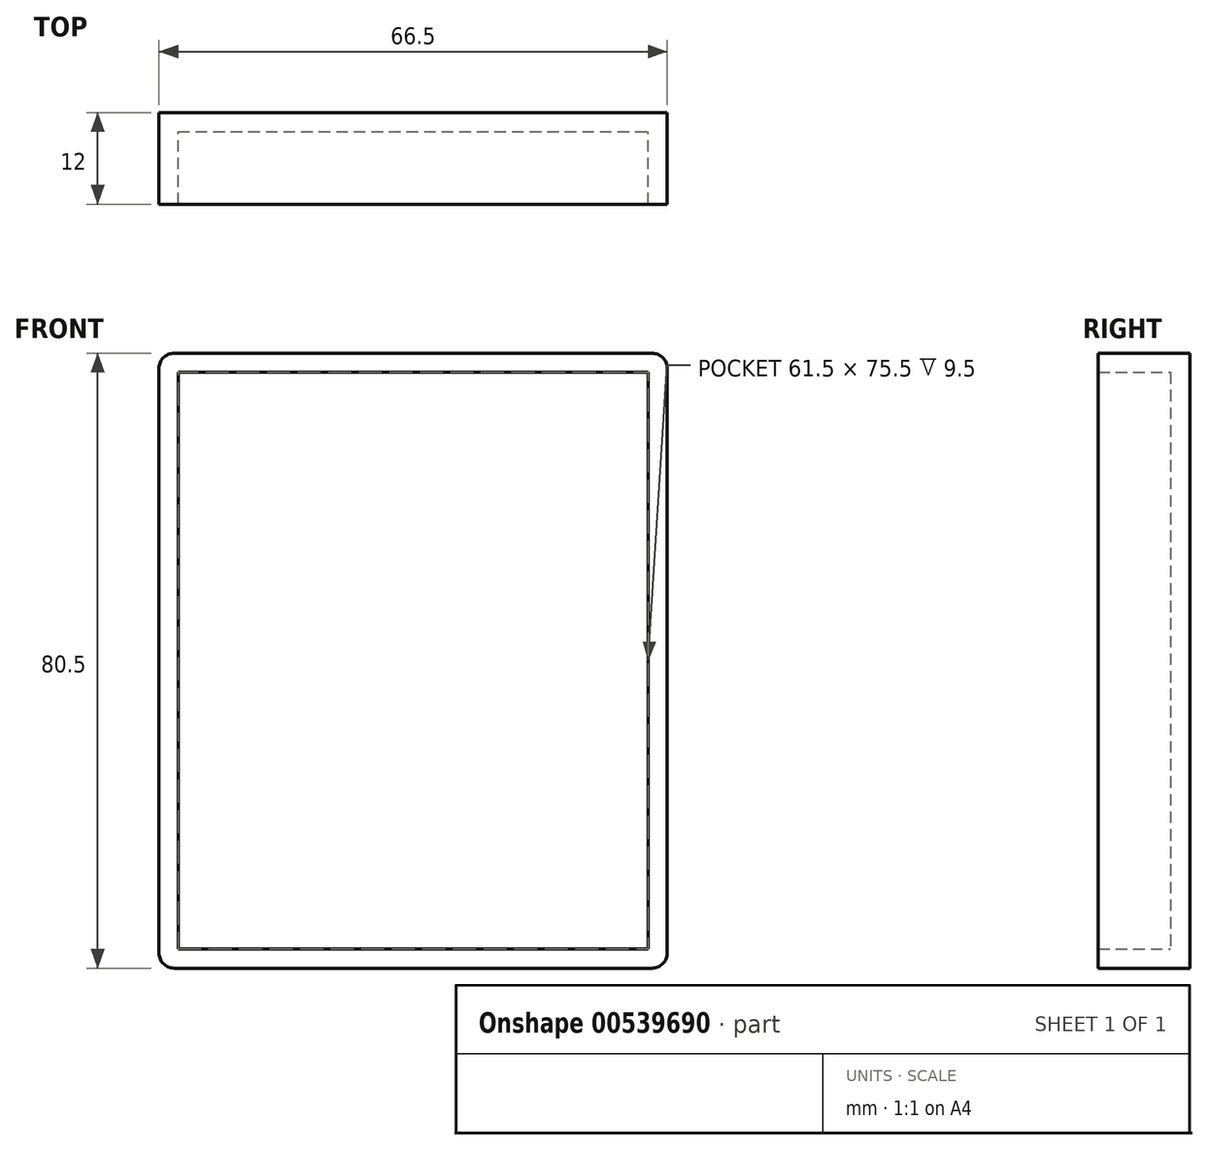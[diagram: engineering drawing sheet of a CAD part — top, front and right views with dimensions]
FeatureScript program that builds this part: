
annotation { "Feature Type Name" : "Feature", "Feature Type Description" : "" }
export const myFeature = defineFeature(function(context is Context, id is Id, definition is map)
    precondition{}
    {
        {
            var Q0;
            Q0=qCreatedBy(makeId("Front.planeOp"),FACE);
            var sketch = newSketch(context, id + "F0", { "sketchPlane" : qUnion([Q0])});
            skLineSegment(sketch, "E0.bottom", {"start": v(-2.5, 78) * mm, "end": v(64, 78) * mm});
            skLineSegment(sketch, "E0.top", {"start": v(-2.5, -2.5) * mm, "end": v(64, -2.5) * mm});
            skLineSegment(sketch, "E0.left", {"start": v(-2.5, 78) * mm, "end": v(-2.5, -2.5) * mm});
            skLineSegment(sketch, "E0.right", {"start": v(64, 78) * mm, "end": v(64, -2.5) * mm});
            skSolve(sketch);
        }
        {
            var Q0;
            Q0=qSketchRegion(id+"F0",true);
            var Q1;
            Q1=makeQuery(id+"F0.imprint","IMPRINT",FACE,{"disambiguationData":[TD([[makeQuery(id+"F0.imprint","IMPRINT",EDGE,{"derivedFrom":sQuery(id+"F0.wireOp",EDGE,"E0.bottom")}),-1.0]])]});
            extrude(context, id + "F1", {"entities" : qUnion([Q0, Q1]), "depth" : 12 * mm, "offsetDistance" : 25 * mm});
        }
        {
            var Q0;
            Q0=makeQuery(id+"F1.opExtrude","CAP_FACE",FACE,{"disambiguationData":[OSD([sQuery(id+"F0.wireOp",EDGE,"E0.bottom"),sQuery(id+"F0.wireOp",EDGE,"E0.top"),sQuery(id+"F0.wireOp",EDGE,"E0.left"),sQuery(id+"F0.wireOp",EDGE,"E0.right")])],"isStart":false});
            shell(context, id + "F2", {"entities" : qUnion([Q0]), "thickness" : 2.5 * mm});
        }
        {
            var Q0;
            Q0=makeQuery(id+"F1.opExtrude","SWEPT_EDGE",EDGE,{"disambiguationData":[OSD([sQuery(id+"F0.wireOp",EDGE,"E0.bottom"),sQuery(id+"F0.wireOp",EDGE,"E0.right")])]});
            var Q1;
            Q1=makeQuery(id+"F1.opExtrude","SWEPT_EDGE",EDGE,{"disambiguationData":[OSD([sQuery(id+"F0.wireOp",EDGE,"E0.bottom"),sQuery(id+"F0.wireOp",EDGE,"E0.left")])]});
            var Q2;
            Q2=makeQuery(id+"F1.opExtrude","SWEPT_EDGE",EDGE,{"disambiguationData":[OSD([sQuery(id+"F0.wireOp",EDGE,"E0.top"),sQuery(id+"F0.wireOp",EDGE,"E0.right")])]});
            var Q3;
            Q3=makeQuery(id+"F1.opExtrude","SWEPT_EDGE",EDGE,{"disambiguationData":[OSD([sQuery(id+"F0.wireOp",EDGE,"E0.top"),sQuery(id+"F0.wireOp",EDGE,"E0.left")])]});
            fillet(context, id + "F3", {"entities" : qUnion([Q0, Q1, Q2, Q3]), "radius" : 2 * mm, "tangentPropagation" : true, "allowEdgeOverflow" : false});
        }
    });
